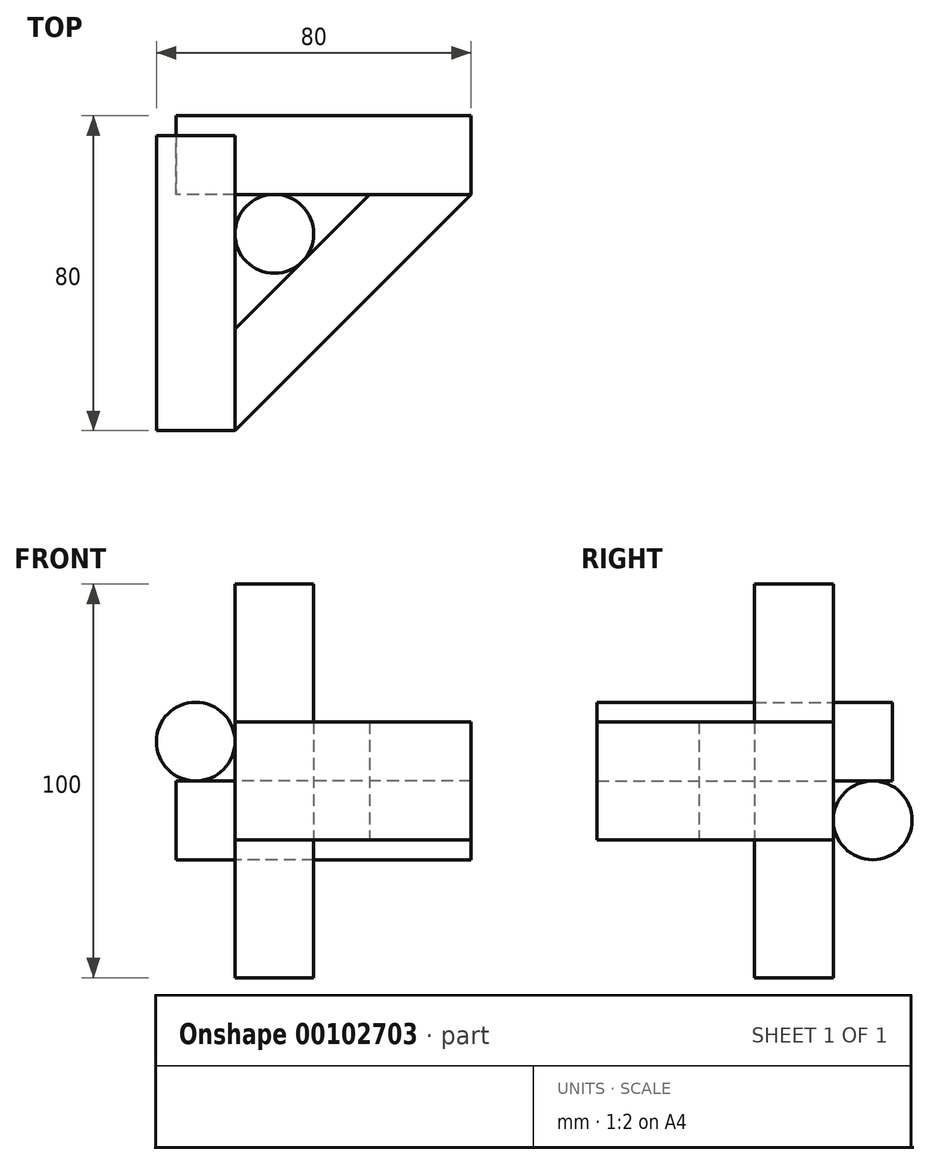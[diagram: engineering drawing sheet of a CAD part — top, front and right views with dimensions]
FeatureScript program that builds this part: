
annotation { "Feature Type Name" : "Feature", "Feature Type Description" : "" }
export const myFeature = defineFeature(function(context is Context, id is Id, definition is map)
    precondition{}
    {
        {
            var Q0;
            Q0=qCreatedBy(makeId("Top.planeOp"),FACE);
            var sketch = newSketch(context, id + "F0", { "sketchPlane" : qUnion([Q0])});
            skCircle(sketch, "E0", {"center": v(0, 0) * mm, "radius": 10 * mm});
            skSolve(sketch);
        }
        {
            var Q0;
            Q0 = qSketchRegion(id + "F0", true);
            extrude(context, id + "F1", {"entities" : qUnion([Q0]), "endBound" : BoundingType.SYMMETRIC, "depth" : 100 * mm});
        }
        {
            var Q0;
            Q0=qCreatedBy(makeId("Front.planeOp"),FACE);
            var sketch = newSketch(context, id + "F2", { "sketchPlane" : qUnion([Q0])});
            skCircle(sketch, "E1", {"center": v(-20, 10) * mm, "radius": 10 * mm});
            skLineSegment(sketch, "E2", {"start": v(-10, -50) * mm, "end": v(-10, 50) * mm, "construction": true});
            skSolve(sketch);
        }
        {
            var Q0;
            Q0 = qSketchRegion(id + "F2", true);
            extrude(context, id + "F3", {"entities" : qUnion([Q0]), "depth" : 50 * mm, "hasSecondDirection" : true, "secondDirectionOppositeDirection" : true, "secondDirectionDepth" : 25 * mm});
        }
        {
            var Q0;
            Q0=qCreatedBy(makeId("Right.planeOp"),FACE);
            var sketch = newSketch(context, id + "F4", { "sketchPlane" : qUnion([Q0])});
            skCircle(sketch, "E3", {"center": v(20, -10) * mm, "radius": 10 * mm});
            skLineSegment(sketch, "E4", {"start": v(-10, -50) * mm, "end": v(-10, 50) * mm, "construction": true});
            skLineSegment(sketch, "E5", {"start": v(10, 50) * mm, "end": v(10, -50) * mm, "construction": true});
            skSolve(sketch);
        }
        {
            var Q0;
            Q0 = qSketchRegion(id + "F4", true);
            extrude(context, id + "F5", {"entities" : qUnion([Q0]), "depth" : 50 * mm, "hasSecondDirection" : true, "secondDirectionOppositeDirection" : true, "secondDirectionDepth" : 25 * mm});
        }
        {
            var Q0;
            Q0=qCreatedBy(makeId("Top.planeOp"),FACE);
            var sketch = newSketch(context, id + "F6", { "sketchPlane" : qUnion([Q0])});
            skLineSegment(sketch, "E6", {"start": v(50, 10) * mm, "end": v(-25, 10) * mm, "construction": true});
            skLineSegment(sketch, "E7", {"start": v(-10, 25) * mm, "end": v(-10, -50) * mm, "construction": true});
            skCircle(sketch, "E8.0", {"center": v(0, 0) * mm, "radius": 10 * mm, "construction": true});
            skLineSegment(sketch, "E9", {"start": v(24.14, 10) * mm, "end": v(-10, -24.14) * mm});
            skLineSegment(sketch, "E10", {"start": v(-10, -24.14) * mm, "end": v(-10, -50) * mm});
            skLineSegment(sketch, "E11", {"start": v(-10, -50) * mm, "end": v(50, 10) * mm});
            skLineSegment(sketch, "E12", {"start": v(24.14, 10) * mm, "end": v(50, 10) * mm});
            skSolve(sketch);
        }
        {
            var Q0;
            Q0 = qSketchRegion(id + "F6", true);
            extrude(context, id + "F7", {"entities" : qUnion([Q0]), "endBound" : BoundingType.SYMMETRIC, "depth" : 30 * mm});
        }
    });
